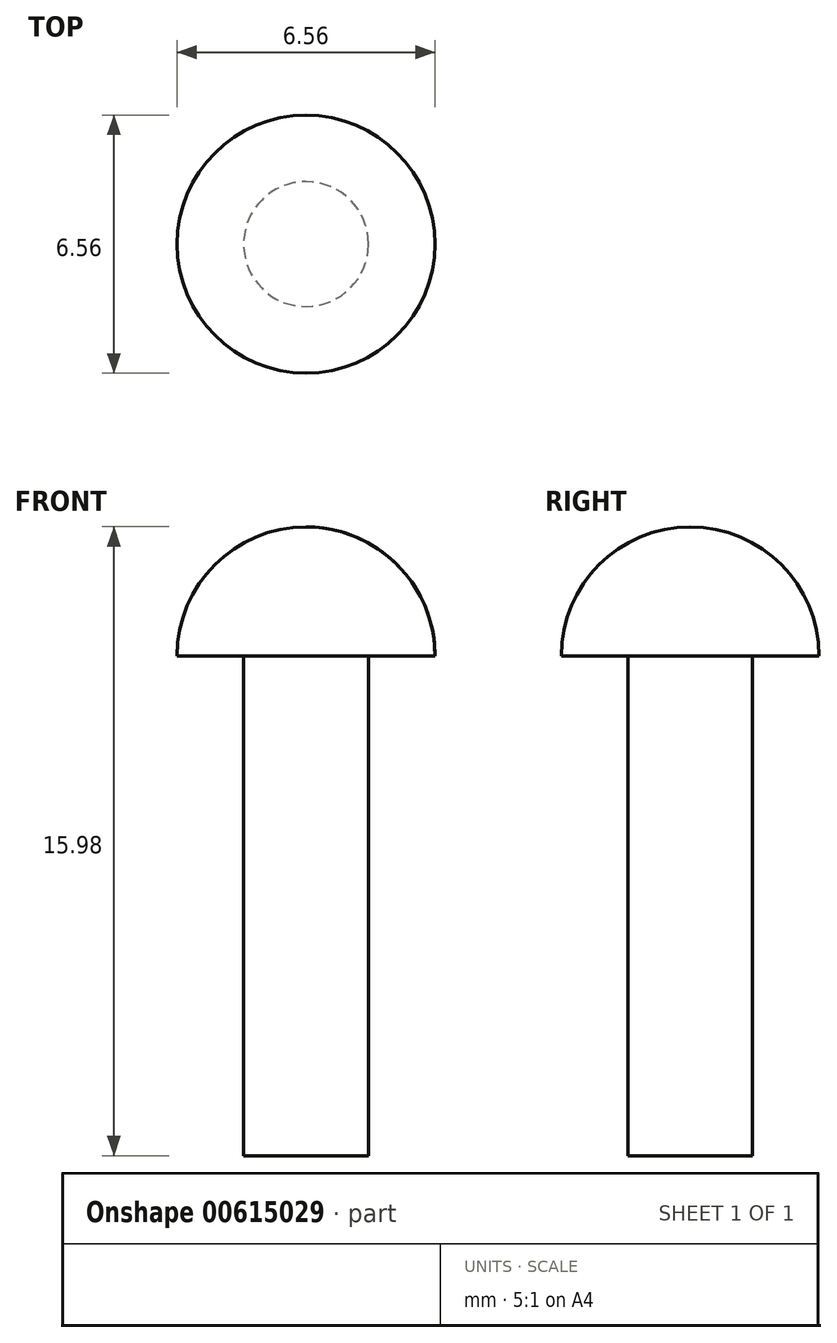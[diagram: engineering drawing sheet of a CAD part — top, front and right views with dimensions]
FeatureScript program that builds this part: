
annotation { "Feature Type Name" : "Feature", "Feature Type Description" : "" }
export const myFeature = defineFeature(function(context is Context, id is Id, definition is map)
    precondition{}
    {
        {
            var Q0;
            Q0=qCreatedBy(makeId("Front.planeOp"),FACE);
            var sketch = newSketch(context, id + "F0", { "sketchPlane" : qUnion([Q0])});
            skLineSegment(sketch, "E0", {"start": v(0, 0) * mm, "end": v(0, 12.7) * mm});
            skLineSegment(sketch, "E1", {"start": v(1.59, 12.7) * mm, "end": v(1.59, 0) * mm});
            skLineSegment(sketch, "E2", {"start": v(1.59, 0) * mm, "end": v(0, 0) * mm});
            skLineSegment(sketch, "E3", {"start": v(0, 12.7) * mm, "end": v(0, 15.98) * mm});
            skArc(sketch, "E4", {"start": v(0, 15.98) * mm, "mid": v(2.32, 15.02) * mm, "end": v(3.28, 12.7) * mm});
            skLineSegment(sketch, "E5", {"start": v(1.59, 12.7) * mm, "end": v(3.28, 12.7) * mm});
            skSolve(sketch);
        }
        {
            var Q0;
            Q0 = qSketchRegion(id + "F0", true);
            var Q1;
            Q1=sQuery(id+"F0.wireOp",EDGE,"E0");
            revolve(context, id + "F1", {"entities" : qUnion([Q0]), "axis" : qUnion([Q1]), "revolveType" : RevolveType.FULL});
        }
    });
